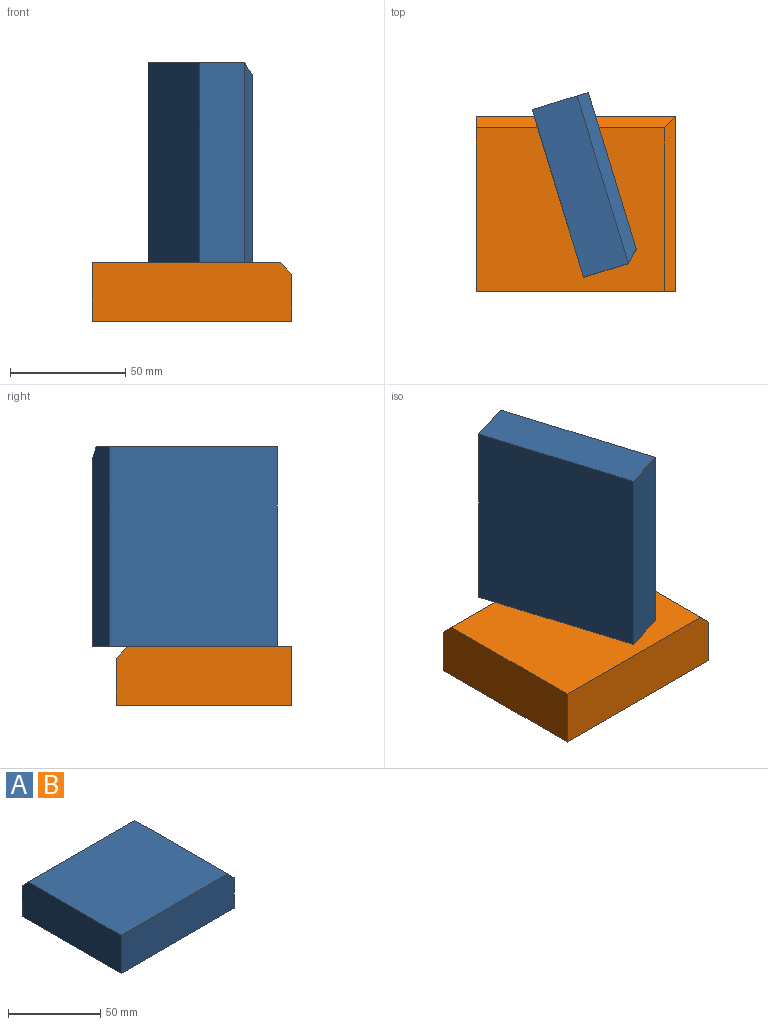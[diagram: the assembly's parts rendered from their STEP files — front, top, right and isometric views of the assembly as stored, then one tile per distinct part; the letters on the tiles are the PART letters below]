
ASSEMBLY  parts=2 mates=1
PART A: 8 faces, bbox 86.5x75.9x25.4 mm
  f0: plane 75.88x25.4mm, normal (-1,0,0), area 1914.4mm2, adj f1,f3,f4,f5,f7
  f1: plane 86.53x25.4mm, normal (0,-1,0), area 2185mm2, adj f0,f2,f4,f5,f6
  f2: plane 75.88x20.32mm, normal (1,0,0), area 1541.9mm2, adj f1,f3,f5,f6
  f3: plane 86.53x20.32mm, normal (0,1,0), area 1758.3mm2, adj f0,f2,f5,f7
  f4: plane 81.45x70.8mm, normal (0,0,1), area 5766.8mm2, adj f0,f1,f6,f7
  f5: plane 86.53x75.88mm, normal (0,0,-1), area 6566mm2, adj f0,f1,f2,f3
  f6: plane 75.88x5.08mm, normal (0.71,0,0.71), area 526.9mm2, adj f1,f2,f4,f7
  f7: plane 86.53x5.08mm, normal (0,0.71,0.71), area 603.4mm2, adj f0,f3,f4,f6
PART B: same geometry as A
PLACE A rot(axis=(-0.7,-0.11,-0.7),168deg) t=(-6.26,10.04,46.42)mm
PLACE B t=(5.69,-0.72,-25.4)mm
MATE planar A.f0 <-> B.f4  axis (0,0,-1) through (6.69,10.85,0)mm
